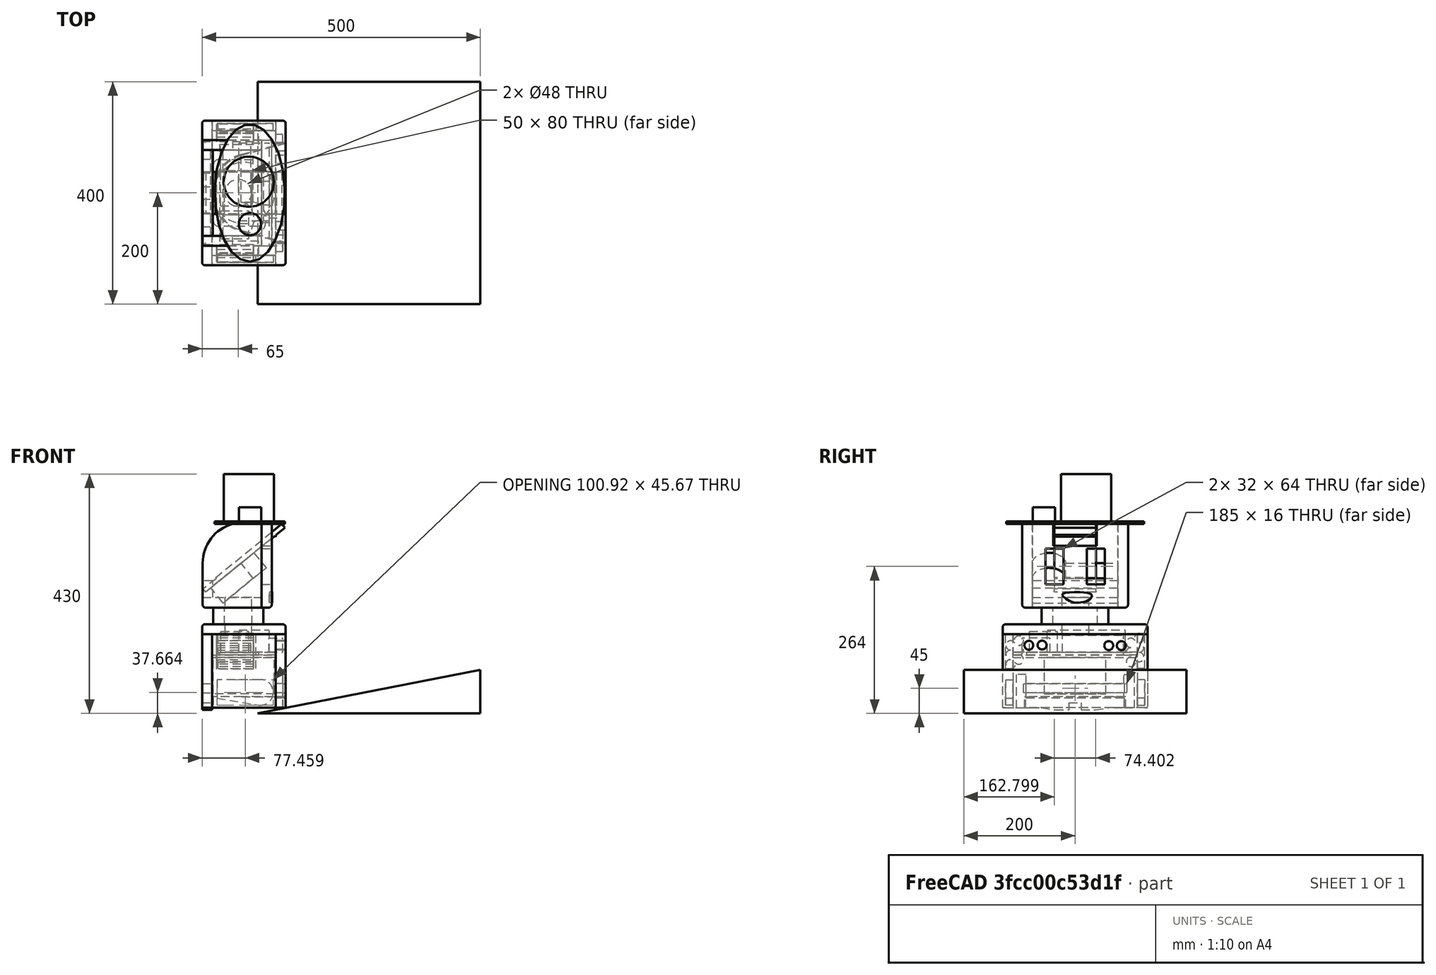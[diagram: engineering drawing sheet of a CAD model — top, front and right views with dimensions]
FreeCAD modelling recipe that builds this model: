
FCSTD DOCUMENT  (FreeCAD 0.17R13541 (Git))
Label: robot secondaire
License: All rights reserved
LicenseURL: http://en.wikipedia.org/wiki/All_rights_reserved
objects: Sketcher::SketchObject×22, PartDesign::Pad×21, TechDraw::DrawViewDimension×21, PartDesign::Body×20, TechDraw::DrawProjGroupItem×9, TechDraw::DrawProjGroup×9, PartDesign::Fillet×8, Part::Box×6, Part::Cylinder×5, PartDesign::FeatureBase×4, Part::Mirroring×1, App::DocumentObjectGroup×1, TechDraw::DrawSVGTemplate×1, TechDraw::DrawPage×1, PartDesign::Pocket×1
note: 110 computed .brp shape members not serialized (recipe doc carries the construction recipe); baked Part::Feature solids carry a one-line shape summary decoded from their .brp

FEATURE [Part::Cylinder] Cylinder  label="Arrêt urgence"
  Angle = 360
  AttacherType = Attacher::AttachEngine3D
  Height = 30
  Placement = pos=(86,-56,340) rot=(0,0,1;0rad)
  Radius = 20
FEATURE [Part::Cylinder] Cylinder001  label="Support balise"
  Angle = 360
  AttacherType = Attacher::AttachEngine3D
  Height = 90
  Placement = pos=(84,20,340) rot=(0,0,1;0rad)
  Radius = 45
FEATURE [Sketcher::SketchObject] Sketch002  label="Face avant002"
  AttachmentOffset = pos=(0,0,132) rot=(0,0,1;0rad)
  MapMode = 2
  Placement = pos=(132,0,0) rot=(0.57735,0.57735,0.57735;2.0944rad)
  sketch-geometry (17):
    g0: LineSegment StartX=-130 StartY=10 StartZ=0 EndX=-130 EndY=142 EndZ=0
    g1: LineSegment StartX=-130 StartY=142 StartZ=0 EndX=130 EndY=142 EndZ=0
    g2: LineSegment StartX=130 StartY=142 StartZ=0 EndX=130 EndY=10 EndZ=0
    g3: LineSegment StartX=130 StartY=10 StartZ=0 EndX=88.5 EndY=10 EndZ=0
    g4: LineSegment StartX=88.5 StartY=53 StartZ=0 EndX=-88.5 EndY=53 EndZ=0
    g5: LineSegment StartX=-88.5 StartY=53 StartZ=0 EndX=-88.5 EndY=37 EndZ=0
    g6: LineSegment StartX=88.5 StartY=53 StartZ=0 EndX=88.5 EndY=37 EndZ=0
    g7: LineSegment StartX=88.5 StartY=37 StartZ=0 EndX=-88.5 EndY=37 EndZ=0
    g8: LineSegment StartX=-88.5 StartY=10 StartZ=0 EndX=-88.5 EndY=28 EndZ=0
    g9: LineSegment StartX=-88.5 StartY=28 StartZ=0 EndX=88.5 EndY=28 EndZ=0
    g10: LineSegment StartX=88.5 StartY=28 StartZ=0 EndX=88.5 EndY=10 EndZ=0
    g11: Circle CenterX=-83.2022 CenterY=122.196 CenterZ=0 NormalX=0 NormalY=0 NormalZ=1 AngleXU=0 Radius=8
    g12: Circle CenterX=-59.3183 CenterY=122.573 CenterZ=0 NormalX=0 NormalY=0 NormalZ=1 AngleXU=0 Radius=8
    g13: Circle CenterX=60.4116 CenterY=121.713 CenterZ=0 NormalX=0 NormalY=0 NormalZ=1 AngleXU=0 Radius=8
    g14: Circle CenterX=82.9519 CenterY=121.552 CenterZ=0 NormalX=0 NormalY=0 NormalZ=1 AngleXU=0 Radius=8
    g15: LineSegment StartX=-130 StartY=10 StartZ=0 EndX=-88.5 EndY=10 EndZ=0
    g16: LineSegment StartX=-130 StartY=100 StartZ=0 EndX=130 EndY=100 EndZ=0
  constraints (41):
    c: Vertical(g0)
    c: Horizontal(g1)
    c: Coincident(g1,g2)
    c: Vertical(g2)
    c: Coincident(g2,g3)
    c: Horizontal(g3)
    c: DistanceY(g0,g0) = 132
    c: Symmetric(g4,g4,g-2)
    c: DistanceX(g1,g1) = 260
    c: Equal(g0,g2)
    c: DistanceX(g4,g4) = 177
    c: Coincident(g5,g4)
    c: Vertical(g5)
    c: Coincident(g6,g4)
    c: Vertical(g6)
    c: Coincident(g7,g6)
    c: Coincident(g7,g5)
    c: Horizontal(g7)
    c: Vertical(g8)
    c: Horizontal(g9)
    c: Coincident(g10,g9)
    c: Coincident(g10,g3)
    c: Vertical(g10)
    c: Equal(g4,g7)
    c: Coincident(g9,g8)
    c: Symmetric(g9,g8,g-2)
    c: Radius(g11) = 8
    c: Coincident(g0,g1)
    c: Coincident(g15,g0)
    c: Coincident(g15,g8)
    c: Horizontal(g15)
    c: Equal(g15,g3)
    c: DistanceY(g-1,g8) = 10
    c: PointOnObject(g16,g0)
    c: PointOnObject(g16,g2)
    c: Horizontal(g16)
    c: DistanceY(g-1,g16) = 100
    c: DistanceY(g4,g16) = 47
    c: DistanceY(g6,g16) = 63
    c: DistanceY(g-1,g9) = 28
    c: Equal(g9,g4)
FEATURE [Part::Cylinder] Cylinder002  label="Oreille"
  Angle = 360
  AttacherType = Attacher::AttachEngine3D
  Height = 5
  Placement = pos=(76,100,290) rot=(1,0,0;1.5708rad)
  Radius = 30
FEATURE [Sketcher::SketchObject] Sketch003  label="Bouche002"
  AttachmentOffset = pos=(0,5,-10) rot=(0,0,1;0rad)
  MapMode = 5
  Placement = pos=(-10,2e-12,5) rot=(0.57735,0.57735,0.57735;2.0944rad)
  Support = -> [YZ_Plane001]
  sketch-geometry (13):
    g0-g6: Circle [constr] x7 (B-spline internal-alignment scaffolding for g7; pole/knot coordinates omitted)
    g7: BSplineCurve PolesCount=7 KnotsCount=5 Degree=3 IsPeriodic=0
    g8-g12: GeomPoint [constr] x5 (B-spline internal-alignment scaffolding for g7; pole/knot coordinates omitted)
  constraints (5):
    c: Radius(g0) = 4
    c: Equal(g0, g1-g6) x6
    c: Coincident(g6,g0)
    c: InternalAlignment(g0-g6 -> g7) x7
    c: InternalAlignment(g8-g12 -> g7) x5
FEATURE [Part::Box] Box005  label="Oeil"
  AttacherType = Attacher::AttachEngine3D
  Height = 64.5
  Length = 25
  Placement = pos=(103,-53,232) rot=(0,0,1;0rad)
  Width = 32
FEATURE [Sketcher::SketchObject] Sketch004  label="Chapeau002"
  AttachmentOffset = pos=(0,0,340) rot=(0,0,1;0rad)
  MapMode = 5
  Placement = pos=(0,0,340) rot=(0,0,1;0rad)
  Support = -> [XY_Plane002]
  sketch-geometry (5):
    g0: Ellipse CenterX=85.6089 CenterY=0 CenterZ=0 NormalX=0 NormalY=0 NormalZ=1 MajorRadius=123.648 MinorRadius=62.9342 AngleXU=-1.5708
    g1: LineSegment [constr] StartX=85.6089 StartY=-123.648 StartZ=0 EndX=85.6089 EndY=123.648 EndZ=0
    g2: LineSegment [constr] StartX=148.543 StartY=0 StartZ=0 EndX=22.6748 EndY=0 EndZ=0
    g3: GeomPoint X=85.6089 Y=-106.433 Z=0
    g4: GeomPoint X=85.6089 Y=106.433 Z=0
  constraints (3):
    c: InternalAlignment(g1-g4 -> g0) x4
    c: Horizontal(g2)
    c: PointOnObject(g0,g-1)
FEATURE [PartDesign::Pad] Pad  label="Chapeau001"
  Length = 5
  Length2 = 100
  Profile = -> Sketch004
  Type = 0
FEATURE [PartDesign::Body] Body002  label="Chapeau"
  Group = -> [Sketch004,Pad]
  Origin = -> Origin002
  Tip = -> Pad
FEATURE [PartDesign::Pad] Pad002  label="Face avant001"
  Length = 18
  Length2 = 100
  Placement = pos=(132,0,0) rot=(0.57735,0.57735,0.57735;2.0944rad)
  Profile = -> Sketch002
  Type = 0
FEATURE [PartDesign::Pad] Pad003  label="Bouche001"
  Length = 5
  Length2 = 100
  Placement = pos=(0,0,0) rot=(0.57735,0.57735,0.57735;2.0944rad)
  Profile = -> Sketch003
  Type = 0
FEATURE [PartDesign::Body] Body001  label="Bouche"
  Group = -> [Sketch003,Pad003]
  Origin = -> Origin001
  Placement = pos=(131,0,0) rot=(0,0,1;0rad)
  Tip = -> Pad003
FEATURE [Sketcher::SketchObject] Sketch005  label="Téléphone002"
  AttachmentOffset = pos=(2,0,0) rot=(0,0,1;0rad)
  MapMode = 5
  Placement = pos=(2,0,0) rot=(1,0,0;1.5708rad)
  Support = -> [XZ_Plane004]
  sketch-geometry (13):
    g0: LineSegment StartX=4.40524 StartY=217.84 StartZ=0 EndX=0 EndY=223.28 EndZ=0
    g1: LineSegment StartX=22.0557 StartY=243.714 StartZ=0 EndX=140.959 EndY=340 EndZ=0
    g2: LineSegment StartX=140.959 StartY=340 StartZ=0 EndX=146.623 EndY=333.006 EndZ=0
    g3: LineSegment StartX=128.749 StartY=318.531 StartZ=0 EndX=4.40524 EndY=217.84 EndZ=0
    g4: LineSegment StartX=128.749 StartY=318.531 StartZ=0 EndX=129.378 EndY=317.754 EndZ=0
    g5: LineSegment StartX=129.378 StartY=317.754 StartZ=0 EndX=131.709 EndY=319.642 EndZ=0
    g6: LineSegment StartX=131.709 StartY=319.642 StartZ=0 EndX=131.08 EndY=320.419 EndZ=0
    g7: LineSegment StartX=131.08 StartY=320.419 StartZ=0 EndX=146.623 EndY=333.006 EndZ=0
    g8: LineSegment [constr] StartX=128.909 StartY=320.717 StartZ=0 EndX=179.705 EndY=0 EndZ=0
    g9: LineSegment [constr] StartX=128.909 StartY=320.717 StartZ=0 EndX=964.406 EndY=0 EndZ=0
    g10: LineSegment [constr] StartX=128.909 StartY=320.717 StartZ=0 EndX=130.544 EndY=318.698 EndZ=0
    g11: LineSegment StartX=22.0557 StartY=243.714 StartZ=0 EndX=23.3144 EndY=242.16 EndZ=0
    g12: LineSegment StartX=23.3144 StartY=242.16 StartZ=0 EndX=0 EndY=223.28 EndZ=0
  constraints (40):
    c: Coincident(g1,g2)
    c: Parallel(g1,g3)
    c: Parallel(g0,g2)
    c: Perpendicular(g1,g0)
    c: Coincident(g3,g0)
    c: Coincident(g3,g4)
    c: Coincident(g4,g5)
    c: Coincident(g5,g6)
    c: Coincident(g6,g7)
    c: Coincident(g7,g2)
    c: Parallel(g7,g1)
    c: Parallel(g5,g1)
    c: Distance(g5) = 3
    c: Perpendicular(g7,g6)
    c: Perpendicular(g4,g3)
    c: Equal(g6,g4)
    c: Distance(g6) = 1
    c: Distance(g7) = 20
    c: Coincident(g9,g8)
    c: Angle(g8,g9) = 1.0472
    c: PointOnObject(g5,g9)
    c: PointOnObject(g4,g8)
    c: Coincident(g10,g8)
    c: PointOnObject(g10,g5)
    c: Perpendicular(g10,g5)
    c: Symmetric(g5,g5,g10)
    c: Coincident(g12,g11)
    c: Perpendicular(g1,g11)
    c: Coincident(g1,g11)
    c: Distance(g2) = 9
    c: Coincident(g0,g12)
    c: Parallel(g12,g3)
    c: Distance(g12) = 30
    c: Distance(g0) = 7
    c: Distance(g1) = 153
    c: Angle(g-1,g3) = 0.680678
    c: DistanceY(g-1,g1) = 340
    c: PointOnObject(g0,g-2)
    c: PointOnObject(g9,g-1)
    c: PointOnObject(g8,g-1)
FEATURE [PartDesign::Pad] Pad004  label="Téléphone001"
  Length = 75
  Length2 = 100
  Midplane = true
  Placement = pos=(0,0,0) rot=(1,0,0;1.5708rad)
  Profile = -> Sketch005
  Type = 0
FEATURE [PartDesign::Body] Body004  label="Téléphone"
  Group = -> [Sketch005,Pad004]
  Origin = -> Origin004
  Tip = -> Pad004
FEATURE [Sketcher::SketchObject] Sketch006  label="Cou002"
  AttachmentOffset = pos=(0,0,160) rot=(0,0,1;0rad)
  MapMode = 5
  Placement = pos=(0,0,160) rot=(0,0,1;0rad)
  Support = -> [XY_Plane005]
  sketch-geometry (8):
    g0: LineSegment StartX=20 StartY=60 StartZ=0 EndX=110 EndY=60 EndZ=0
    g1: LineSegment StartX=110 StartY=60 StartZ=0 EndX=110 EndY=-60 EndZ=0
    g2: LineSegment StartX=110 StartY=-60 StartZ=0 EndX=20 EndY=-60 EndZ=0
    g3: LineSegment StartX=20 StartY=-60 StartZ=0 EndX=20 EndY=60 EndZ=0
    g4: LineSegment StartX=40 StartY=40 StartZ=0 EndX=90 EndY=40 EndZ=0
    g5: LineSegment StartX=90 StartY=40 StartZ=0 EndX=90 EndY=-40 EndZ=0
    g6: LineSegment StartX=90 StartY=-40 StartZ=0 EndX=40 EndY=-40 EndZ=0
    g7: LineSegment StartX=40 StartY=-40 StartZ=0 EndX=40 EndY=40 EndZ=0
  constraints (24):
    c: Coincident(g0,g1)
    c: Coincident(g1,g2)
    c: Coincident(g2,g3)
    c: Coincident(g3,g0)
    c: Horizontal(g0)
    c: Horizontal(g2)
    c: Vertical(g1)
    c: Vertical(g3)
    c: Coincident(g4,g5)
    c: Coincident(g5,g6)
    c: Coincident(g6,g7)
    c: Coincident(g7,g4)
    c: Horizontal(g4)
    c: Horizontal(g6)
    c: Vertical(g5)
    c: Vertical(g7)
    c: DistanceX(g0,g4) = 20
    c: DistanceX(g4,g0) = 20
    c: DistanceX(g0,g0) = 90
    c: DistanceY(g1,g1) = 120
    c: DistanceY(g4,g0) = 20
    c: Symmetric(g0,g2,g-1)
    c: DistanceX(g-1,g0) = 20
    c: DistanceY(g1,g5) = 20
FEATURE [PartDesign::Pad] Pad005  label="Cou001"
  Length = 30
  Length2 = 100
  Profile = -> Sketch006
  Type = 0
FEATURE [PartDesign::Fillet] Fillet003  label="Fillet cou"
  Base = -> Pad005 [Edge5,Edge2,Edge8,Edge1]
  BaseFeature = -> Pad005
  Radius = 10
FEATURE [PartDesign::Body] Body005  label="Cou"
  Group = -> [Sketch006,Pad005,Fillet003]
  Origin = -> Origin005
  Tip = -> Fillet003
FEATURE [Part::Box] Box006  label="Ultrason"
  AttacherType = Attacher::AttachEngine3D
  Height = 25
  Length = 25
  Placement = pos=(120,45,110) rot=(0,0,1;0rad)
  Width = 50
FEATURE [Part::Mirroring] Part__Mirroring003  label="Ultrason (Mirror)"
  Base = (0,0,0)
  Normal = (0,1,0)
  Source = -> Box006
FEATURE [Part::Box] Box008  label="Pont H"
  AttacherType = Attacher::AttachEngine3D
  Height = 37
  Length = 50
  Placement = pos=(34,-82,110) rot=(0,0,1;0rad)
  Width = 50
FEATURE [Part::Box] Box009  label="Arduino Uno"
  AttacherType = Attacher::AttachEngine3D
  Height = 40
  Length = 55
  Placement = pos=(66,-50,110) rot=(0,0,1;0rad)
  Width = 140
FEATURE [Part::Box] Box010  label="Arduino nano et alim 5V"
  AttacherType = Attacher::AttachEngine3D
  Height = 30
  Length = 55
  Placement = pos=(33,-23,110) rot=(0,0,1;0rad)
  Width = 110
FEATURE [Part::Cylinder] Cylinder003  label="LIDAR"
  Angle = 360
  AttacherType = Attacher::AttachEngine3D
  Height = 65
  Placement = pos=(75,0,35) rot=(0,0,1;0rad)
  Radius = 55
FEATURE [Part::Box] Box011  label="Plaque électronique"
  AttacherType = Attacher::AttachEngine3D
  Height = 5
  Length = 114
  Placement = pos=(18,-112,100) rot=(0,0,1;0rad)
  Width = 224
  expr: Placement.Base.y = Width / -2
FEATURE [Sketcher::SketchObject] Sketch037  label="batterie"
  MapMode = 5
  Placement = pos=(26.5,115,101) rot=(0.707107,0,0.707107;3.14159rad)
  expr: Constraints[27] = batterie.Constraints.pileRayon * 2
  expr: Constraints.pileRayon = 33.899999999999999 / 4
  sketch-geometry (12):
    g0: ArcOfCircle CenterX=33.9 CenterY=0 CenterZ=0 NormalX=0 NormalY=0 NormalZ=1 AngleXU=0 Radius=8.475 StartAngle=3.14159 EndAngle=8.37758
    g1: ArcOfCircle CenterX=8.475 CenterY=14.6791 CenterZ=0 NormalX=0 NormalY=0 NormalZ=1 AngleXU=0 Radius=8.475 StartAngle=6.072e-09 EndAngle=3.14159
    g2: ArcOfCircle CenterX=25.425 CenterY=14.6791 CenterZ=0 NormalX=0 NormalY=0 NormalZ=1 AngleXU=0 Radius=8.475 StartAngle=5.23599 EndAngle=9.42478
    g3: ArcOfCircle CenterX=-8.475 CenterY=14.6791 CenterZ=0 NormalX=0 NormalY=0 NormalZ=1 AngleXU=0 Radius=8.475 StartAngle=6.31e-09 EndAngle=5.23599
    g4: ArcOfCircle CenterX=16.95 CenterY=0 CenterZ=0 NormalX=0 NormalY=0 NormalZ=1 AngleXU=0 Radius=8.475 StartAngle=3.14159 EndAngle=6.28319
    g5: ArcOfCircle CenterX=0 CenterY=0 CenterZ=0 NormalX=0 NormalY=0 NormalZ=1 AngleXU=0 Radius=8.475 StartAngle=2.0944 EndAngle=6.28319
    g6: LineSegment [constr] StartX=33.9 StartY=0 StartZ=0 EndX=25.425 EndY=14.6791 EndZ=0
    g7: LineSegment [constr] StartX=25.425 StartY=14.6791 StartZ=0 EndX=16.95 EndY=0 EndZ=0
    g8: LineSegment [constr] StartX=16.95 StartY=0 StartZ=0 EndX=8.475 EndY=14.6791 EndZ=0
    g9: LineSegment [constr] StartX=8.475 StartY=14.6791 StartZ=0 EndX=0 EndY=0 EndZ=0
    g10: LineSegment [constr] StartX=0 StartY=0 StartZ=0 EndX=-8.475 EndY=14.6791 EndZ=0
    g11: LineSegment [constr] StartX=-8.475 StartY=14.6791 StartZ=0 EndX=25.425 EndY=14.6791 EndZ=0
  constraints (34):
    c: Radius(g0) = 8.475  'pileRayon'
    c: Equal(g0,g1)
    c: Equal(g0,g2)
    c: Equal(g0,g3)
    c: Coincident(g0,g4)
    c: Coincident(g1,g3)
    c: Coincident(g5,g3)
    c: Coincident(g2,g1)
    c: Coincident(g4,g5)
    c: Coincident(g0,g2)
    c: Equal(g4,g5)
    c: Equal(g5,g3)
    c: PointOnObject(g0,g-1)
    c: Coincident(g6,g0)
    c: Coincident(g6,g2)
    c: Coincident(g7,g2)
    c: Coincident(g7,g4)
    c: Coincident(g7,g8)
    c: Coincident(g8,g1)
    c: Coincident(g8,g9)
    c: Coincident(g9,g5)
    c: Coincident(g9,g10)
    c: Coincident(g3,g10)
    c: Parallel(g6,g8)
    c: Parallel(g8,g10)
    c: Parallel(g9,g7)
    c: Coincident(g5,g-1)
    c: Distance(g6) = 16.95
    c: Equal(g6,g7)
    c: Equal(g7,g8)
    c: Equal(g8,g9)
    c: Equal(g9,g10)
    c: Coincident(g11,g3)
    c: Coincident(g11,g2)
FEATURE [PartDesign::Pad] Pad006  label="Batterie"
  Length = 66
  Length2 = 100
  Placement = pos=(26.5,115,101) rot=(0.707107,0,0.707107;3.14159rad)
  Profile = -> Sketch037
  Type = 0
FEATURE [PartDesign::Body] Body006  label="Batterie001"
  Group = -> [Sketch037,Pad006]
  Origin = -> Origin006
  Tip = -> Pad006
FEATURE [PartDesign::FeatureBase] Clone  label="Batterie002"
  BaseFeature = -> Pad006
  Placement = pos=(26.5,-116,122) rot=(0,1,0;1.5708rad)
FEATURE [PartDesign::Body] CloneBody  label="Batterie003"
  BaseFeature = -> Pad006
  Group = -> [Clone]
  Origin = -> Origin008
  Tip = -> Clone
FEATURE [Sketcher::SketchObject] Sketch038  label="porte électronique"
  AttachmentOffset = pos=(0,0,105) rot=(0,0,1;0rad)
  MapMode = 5
  Placement = pos=(0,0,105) rot=(0,0,1;0rad)
  Support = -> [XY_Plane009]
  sketch-geometry (8):
    g0: LineSegment StartX=132 StartY=-112 StartZ=0 EndX=102 EndY=-112 EndZ=0
    g1: LineSegment StartX=102 StartY=-112 StartZ=0 EndX=102 EndY=-87 EndZ=0
    g2: LineSegment StartX=102 StartY=-87 StartZ=0 EndX=32 EndY=-87 EndZ=0
    g3: LineSegment StartX=32 StartY=-87 StartZ=0 EndX=32 EndY=87 EndZ=0
    g4: LineSegment StartX=32 StartY=87 StartZ=0 EndX=102 EndY=87 EndZ=0
    g5: LineSegment StartX=102 StartY=87 StartZ=0 EndX=102 EndY=112 EndZ=0
    g6: LineSegment StartX=102 StartY=112 StartZ=0 EndX=132 EndY=112 EndZ=0
    g7: LineSegment StartX=132 StartY=112 StartZ=0 EndX=132 EndY=-112 EndZ=0
  constraints (24):
    c: Horizontal(g4)
    c: Coincident(g5,g4)
    c: Coincident(g6,g5)
    c: Vertical(g5)
    c: Horizontal(g6)
    c: Coincident(g6,g7)
    c: Vertical(g7)
    c: Coincident(g0,g7)
    c: Coincident(g0,g1)
    c: Coincident(g1,g2)
    c: Vertical(g1)
    c: Horizontal(g0)
    c: Horizontal(g2)
    c: Coincident(g2,g3)
    c: Equal(g5,g1)
    c: Equal(g6,g0)
    c: Equal(g4,g2)
    c: Coincident(g3,g4)
    c: Symmetric(g3,g2,g-1)
    c: DistanceX(g3,g6) = 100
    c: DistanceX(g-1,g6) = 132
    c: DistanceY(g-1,g6) = 112
    c: DistanceY(g5,g5) = 25
    c: DistanceX(g6,g6) = 30
FEATURE [PartDesign::Pad] Pad007
  Length = 5
  Length2 = 100
  Profile = -> Sketch038
  Type = 0
FEATURE [PartDesign::Body] Body007  label="Porte électronique"
  Group = -> [Sketch038,Pad007]
  Origin = -> Origin009
  Tip = -> Pad007
FEATURE [Sketcher::SketchObject] Sketch039  label="Pente002"
  MapMode = 5
  Placement = pos=(0,0,0) rot=(1,0,0;1.5708rad)
  Support = -> [XZ_Plane010]
  sketch-geometry (3):
    g0: LineSegment StartX=100 StartY=0 StartZ=0 EndX=500 EndY=77.7521 EndZ=0
    g1: LineSegment StartX=500 StartY=77.7521 StartZ=0 EndX=500 EndY=0 EndZ=0
    g2: LineSegment StartX=500 StartY=0 StartZ=0 EndX=100 EndY=0 EndZ=0
  constraints (9):
    c: PointOnObject(g0,g-1)
    c: Coincident(g1,g0)
    c: Vertical(g1)
    c: Coincident(g2,g1)
    c: Coincident(g2,g0)
    c: Horizontal(g2)
    c: DistanceX(g2,g2) = 400
    c: Angle(g2,g0) = 0.191986
    c: DistanceX(g-1,g0) = 100
FEATURE [PartDesign::Pad] Pad008  label="Pente001"
  Length = 400
  Length2 = 100
  Midplane = true
  Placement = pos=(0,0,0) rot=(1,0,0;1.5708rad)
  Profile = -> Sketch039
  Type = 0
FEATURE [PartDesign::Body] Body008  label="Pente"
  Group = -> [Sketch039,Pad008]
  Origin = -> Origin010
  Tip = -> Pad008
FEATURE [Sketcher::SketchObject] Sketch040
  AttachmentOffset = pos=(0,0,125) rot=(0,0,1;0rad)
  MapMode = 5
  Placement = pos=(0,-125,-1.3e-11) rot=(1,0,0;1.5708rad)
  Support = -> [XZ_Plane011]
  expr: Constraints[6] = 75 / 2
  expr: Constraints[8] = 45 - 18
  expr: Constraints[10] = 46 / 2
  sketch-geometry (15):
    g0: LineSegment StartX=18 StartY=10 StartZ=0 EndX=132 EndY=10 EndZ=0
    g1: LineSegment StartX=132 StartY=10 StartZ=0 EndX=132 EndY=142 EndZ=0
    g2: Circle [constr] CenterX=105 CenterY=37.5 CenterZ=0 NormalX=0 NormalY=0 NormalZ=1 AngleXU=0 Radius=37.5
    g3: Circle [constr] CenterX=105 CenterY=37.5 CenterZ=0 NormalX=0 NormalY=0 NormalZ=1 AngleXU=0 Radius=23
    g4: LineSegment StartX=105 StartY=60.5 StartZ=0 EndX=27 EndY=60.5 EndZ=0
    g5: ArcOfCircle CenterX=105 CenterY=37.5 CenterZ=0 NormalX=0 NormalY=0 NormalZ=1 AngleXU=0 Radius=23 StartAngle=4.54308 EndAngle=7.85398
    g6: LineSegment [constr] StartX=105 StartY=60.5 StartZ=0 EndX=105 EndY=37.5 EndZ=0
    g7: LineSegment StartX=27 StartY=60.5 StartZ=0 EndX=27 EndY=27.5 EndZ=0
    g8: LineSegment StartX=27 StartY=27.5 StartZ=0 EndX=101.125 EndY=14.8289 EndZ=0
    g9: LineSegment StartX=28 StartY=142 StartZ=0 EndX=28 EndY=80.5 EndZ=0
    g10: LineSegment StartX=28 StartY=80.5 StartZ=0 EndX=97 EndY=80.5 EndZ=0
    g11: LineSegment StartX=97 StartY=80.5 StartZ=0 EndX=97 EndY=142 EndZ=0
    g12: LineSegment StartX=18 StartY=142 StartZ=0 EndX=18 EndY=10 EndZ=0
    g13: LineSegment StartX=18 StartY=142 StartZ=0 EndX=28 EndY=142 EndZ=0
    g14: LineSegment StartX=97 StartY=142 StartZ=0 EndX=132 EndY=142 EndZ=0
  constraints (43):
    c: Horizontal(g0)
    c: Vertical(g1)
    c: Coincident(g1,g0)
    c: DistanceY(g-1,g0) = 10
    c: DistanceX(g0,g0) = 114
    c: DistanceX(g-1,g0) = 18
    c: Radius(g2) = 37.5
    c: DistanceY(g-1,g2) = 37.5
    c: DistanceX(g2,g0) = 27
    c: Coincident(g3,g2)
    c: Radius(g3) = 23
    c: PointOnObject(g4,g3)
    c: Horizontal(g4)
    c: DistanceX(g4,g4) = 78
    c: Coincident(g5,g2)
    c: Coincident(g5,g4)
    c: Coincident(g6,g4)
    c: Coincident(g6,g2)
    c: Vertical(g6)
    c: Coincident(g7,g4)
    c: Vertical(g7)
    c: Coincident(g8,g7)
    c: Coincident(g8,g5)
    c: Tangent(g8,g3)
    c: DistanceY(g7,g7) = 33
    c: Vertical(g9)
    c: DistanceY(g4,g9) = 20
    c: Coincident(g10,g9)
    c: Horizontal(g10)
    c: Vertical(g11)
    c: Coincident(g10,g11)
    c: DistanceX(g10,g10) = 69
    c: Coincident(g12,g0)
    c: Vertical(g12)
    c: Coincident(g13,g12)
    c: Coincident(g13,g9)
    c: Horizontal(g13)
    c: Coincident(g14,g11)
    c: Horizontal(g14)
    c: Coincident(g14,g1)
    c: DistanceY(g1,g1) = 132
    c: Equal(g12,g1)
    c: DistanceX(g13,g13) = 10
FEATURE [Sketcher::SketchObject] Sketch041
  AttachmentOffset = pos=(0,0,125) rot=(0,0,1;0rad)
  MapMode = 5
  Placement = pos=(0,-125,-1.3e-11) rot=(1,0,0;1.5708rad)
  Support = -> [XZ_Plane011]
  sketch-geometry (4):
    g0: LineSegment StartX=18 StartY=10 StartZ=0 EndX=132 EndY=10 EndZ=0
    g1: LineSegment StartX=132 StartY=10 StartZ=0 EndX=132 EndY=142 EndZ=0
    g2: LineSegment StartX=132 StartY=142 StartZ=0 EndX=18 EndY=142 EndZ=0
    g3: LineSegment StartX=18 StartY=142 StartZ=0 EndX=18 EndY=10 EndZ=0
  constraints (12):
    c: Coincident(g0,g1)
    c: Coincident(g1,g2)
    c: Coincident(g2,g3)
    c: Coincident(g3,g0)
    c: Horizontal(g0)
    c: Horizontal(g2)
    c: Vertical(g1)
    c: Vertical(g3)
    c: DistanceY(g3,g3) = 132
    c: DistanceY(g-1,g0) = 10
    c: DistanceX(g-1,g0) = 18
    c: DistanceX(g0,g0) = 114
FEATURE [PartDesign::Pad] Pad009  label="Corps droit interieur"
  Length = 13
  Length2 = 100
  Placement = pos=(0,0,0) rot=(1,0,0;1.5708rad)
  Profile = -> Sketch040
  Reversed = true
  Type = 0
FEATURE [PartDesign::Pad] Pad010  label="Corps droite extérieur"
  BaseFeature = -> Pad009
  Length = 5
  Length2 = 100
  Placement = pos=(0,0,0) rot=(1,0,0;1.5708rad)
  Profile = -> Sketch041
  Type = 0
FEATURE [PartDesign::Body] Body009  label="Corps droite"
  Group = -> [Sketch040,Sketch041,Pad009,Pad010]
  Origin = -> Origin011
  Tip = -> Pad010
FEATURE [Part::Cylinder] Cylinder004  label="Roue001"
  Angle = 360
  AttacherType = Attacher::AttachEngine3D
  Height = 14
  Placement = pos=(105,-90,37.5) rot=(1,0,0;1.5708rad)
  Radius = 37.5
  expr: Placement.Base.z = Radius
  expr: Radius = 75 / 2
FEATURE [Sketcher::SketchObject] Sketch042  label="Face arriere002"
  AttachmentOffset = pos=(0,0,132) rot=(0,0,1;0rad)
  MapMode = 2
  Placement = pos=(0,0,0) rot=(0.57735,0.57735,0.57735;2.0944rad)
  sketch-geometry (17):
    g0: LineSegment StartX=-130 StartY=10 StartZ=0 EndX=-130 EndY=142 EndZ=0
    g1: LineSegment StartX=-130 StartY=142 StartZ=0 EndX=130 EndY=142 EndZ=0
    g2: LineSegment StartX=130 StartY=142 StartZ=0 EndX=130 EndY=10 EndZ=0
    g3: LineSegment StartX=130 StartY=10 StartZ=0 EndX=60.6779 EndY=10 EndZ=0
    g4: LineSegment StartX=-130 StartY=10 StartZ=0 EndX=-60.6779 EndY=10 EndZ=0
    g5: LineSegment StartX=-130 StartY=100 StartZ=0 EndX=130 EndY=100 EndZ=0
    g6: LineSegment StartX=-60.6779 StartY=10 StartZ=0 EndX=-36 EndY=6 EndZ=0
    g7: LineSegment StartX=-11 StartY=19 StartZ=0 EndX=11 EndY=19 EndZ=0
    g8: LineSegment StartX=36 StartY=6 StartZ=0 EndX=60.6779 EndY=10 EndZ=0
    g9: LineSegment StartX=-36 StartY=6 StartZ=0 EndX=-11 EndY=6 EndZ=0
    g10: LineSegment StartX=-11 StartY=6 StartZ=0 EndX=-11 EndY=19 EndZ=0
    g11: LineSegment StartX=11 StartY=19 StartZ=0 EndX=11 EndY=6 EndZ=0
    g12: LineSegment StartX=11 StartY=6 StartZ=0 EndX=36 EndY=6 EndZ=0
    g13: LineSegment StartX=-92.5 StartY=53 StartZ=0 EndX=92.5 EndY=53 EndZ=0
    g14: LineSegment StartX=92.5 StartY=53 StartZ=0 EndX=92.5 EndY=37 EndZ=0
    g15: LineSegment StartX=92.5 StartY=37 StartZ=0 EndX=-92.5 EndY=37 EndZ=0
    g16: LineSegment StartX=-92.5 StartY=37 StartZ=0 EndX=-92.5 EndY=53 EndZ=0
  constraints (52):
    c: Vertical(g0)
    c: Horizontal(g1)
    c: Coincident(g1,g2)
    c: Vertical(g2)
    c: Coincident(g2,g3)
    c: Horizontal(g3)
    c: DistanceY(g0,g0) = 132
    c: DistanceX(g1,g1) = 260
    c: Equal(g0,g2)
    c: Coincident(g0,g1)
    c: Coincident(g4,g0)
    c: Horizontal(g4)
    c: Equal(g4,g3)
    c: DistanceY(g-1,g4) = 10
    c: PointOnObject(g5,g0)
    c: PointOnObject(g5,g2)
    c: Horizontal(g5)
    c: DistanceY(g-1,g5) = 100
    c: Symmetric(g0,g2,g-2)
    c: Horizontal(g7)
    c: Coincident(g8,g3)
    c: Symmetric(g7,g7,g-2)
    c: Coincident(g6,g4)
    c: DistanceY(g-1,g6) = 6
    c: Coincident(g9,g6)
    c: Horizontal(g9)
    c: Coincident(g10,g9)
    c: Coincident(g10,g7)
    c: Coincident(g11,g7)
    c: Coincident(g12,g11)
    c: Coincident(g12,g8)
    c: Horizontal(g12)
    c: Equal(g12,g9)
    c: DistanceX(g9,g9) = 25
    c: Vertical(g10)
    c: Vertical(g11)
    c: Equal(g11,g10)
    c: DistanceX(g7,g7) = 22
    c: Equal(g8,g12)
    c: DistanceY(g11,g11) = 13
    c: Coincident(g13,g14)
    c: Coincident(g14,g15)
    c: Coincident(g15,g16)
    c: Coincident(g16,g13)
    c: Horizontal(g13)
    c: Horizontal(g15)
    c: Vertical(g14)
    c: Vertical(g16)
    c: DistanceY(g13,g5) = 47
    c: DistanceY(g14,g5) = 63
    c: DistanceX(g13,g13) = 185
    c: Symmetric(g13,g13,g-2)
FEATURE [PartDesign::Pad] Pad011  label="Face arriere001"
  Length = 18
  Length2 = 100
  Placement = pos=(0,0,0) rot=(0.57735,0.57735,0.57735;2.0944rad)
  Profile = -> Sketch042
  Type = 0
FEATURE [Sketcher::SketchObject] Sketch043  label="Collecteur palets002"
  AttachmentOffset = pos=(0,0,10) rot=(0,0,1;0rad)
  MapMode = 5
  Placement = pos=(0,0,10) rot=(0,0,1;0rad)
  Support = -> [XY_Plane013]
  expr: Constraints[20] = 72 + 18
  sketch-geometry (8):
    g0: ArcOfCircle CenterX=90 CenterY=0 CenterZ=0 NormalX=0 NormalY=0 NormalZ=1 AngleXU=0 Radius=70 StartAngle=1.8326 EndAngle=4.45059
    g1: ArcOfCircle CenterX=90 CenterY=0 CenterZ=0 NormalX=0 NormalY=0 NormalZ=1 AngleXU=0 Radius=72 StartAngle=1.8326 EndAngle=4.45059
    g2: LineSegment StartX=71.365 StartY=69.5467 StartZ=0 EndX=150 EndY=90.6168 EndZ=0
    g3: LineSegment StartX=150 StartY=90.6168 StartZ=0 EndX=150 EndY=88.6168 EndZ=0
    g4: LineSegment StartX=150 StartY=88.6168 StartZ=0 EndX=71.8827 EndY=67.6148 EndZ=0
    g5: LineSegment StartX=71.8827 StartY=-67.6148 StartZ=0 EndX=150.018 EndY=-88.551 EndZ=0
    g6: LineSegment StartX=150.018 StartY=-88.551 StartZ=0 EndX=150.018 EndY=-90.551 EndZ=0
    g7: LineSegment StartX=150.018 StartY=-90.551 StartZ=0 EndX=71.365 EndY=-69.5467 EndZ=0
  constraints (22):
    c: Symmetric(g0,g0,g-1)
    c: Symmetric(g1,g1,g-1)
    c: Radius(g0) = 70
    c: Radius(g1) = 72
    c: Angle(g0) = 2.61799
    c: Angle(g1) = 2.61799
    c: Coincident(g0,g1)
    c: Tangent(g1,g2) = 1.5708
    c: Coincident(g2,g3)
    c: Coincident(g3,g4)
    c: Coincident(g4,g0)
    c: Vertical(g3)
    c: DistanceY(g3,g3) = 2
    c: Tangent(g0,g5) = -1.5708
    c: Coincident(g5,g6)
    c: Vertical(g6)
    c: Coincident(g6,g7)
    c: Coincident(g7,g1)
    c: Equal(g6,g3)
    c: DistanceX(g-1,g3) = 150
    c: DistanceX(g-1,g0) = 90
    c: Equal(g5,g4)
FEATURE [PartDesign::Pad] Pad012  label="Collecteur palets001"
  Length = 20
  Length2 = 100
  Profile = -> Sketch043
  Type = 0
FEATURE [PartDesign::Body] Body011  label="Collecteur palets"
  Group = -> [Sketch043,Pad012]
  Origin = -> Origin013
  Tip = -> Pad012
FEATURE [Sketcher::SketchObject] Sketch045  label="Face dessus002"
  AttachmentOffset = pos=(0,0,142) rot=(0,0,1;0rad)
  MapMode = 5
  Placement = pos=(0,0,142) rot=(0,0,1;0rad)
  Support = -> [XY_Plane015]
  sketch-geometry (5):
    g0: LineSegment StartX=0 StartY=130 StartZ=0 EndX=150 EndY=130 EndZ=0
    g1: LineSegment StartX=150 StartY=130 StartZ=0 EndX=150 EndY=-130 EndZ=0
    g2: LineSegment StartX=150 StartY=-130 StartZ=0 EndX=0 EndY=-130 EndZ=0
    g3: LineSegment StartX=0 StartY=-130 StartZ=0 EndX=0 EndY=130 EndZ=0
    g4: Circle CenterX=65 CenterY=0 CenterZ=0 NormalX=0 NormalY=0 NormalZ=1 AngleXU=0 Radius=24
  constraints (15):
    c: Coincident(g0,g1)
    c: Coincident(g1,g2)
    c: Coincident(g2,g3)
    c: Coincident(g3,g0)
    c: Horizontal(g0)
    c: Horizontal(g2)
    c: Vertical(g1)
    c: Vertical(g3)
    c: PointOnObject(g0,g-2)
    c: Symmetric(g0,g2,g-1)
    c: DistanceY(g3,g3) = 260
    c: DistanceX(g0,g0) = 150
    c: PointOnObject(g4,g-1)
    c: Radius(g4) = 24
    c: DistanceX(g-1,g4) = 65
FEATURE [PartDesign::Pad] Pad013  label="Face dessus001"
  Length = 18
  Length2 = 100
  Profile = -> Sketch045
  Type = 0
FEATURE [PartDesign::Fillet] Fillet007  label="Fillet Face dessus"
  Base = -> Pad013 [Edge10,Edge7,Edge4,Edge12,Edge8,Edge5,Edge1,Edge2]
  BaseFeature = -> Pad013
  Radius = 5
FEATURE [PartDesign::Body] Body013  label="Face dessus"
  Group = -> [Sketch045,Pad013,Fillet007]
  Origin = -> Origin015
  Tip = -> Fillet007
FEATURE [Sketcher::SketchObject] Sketch046  label="Dessous tete002"
  AttachmentOffset = pos=(0,0,190) rot=(0,0,1;0rad)
  MapMode = 5
  Placement = pos=(0,0,190) rot=(0,0,1;0rad)
  Support = -> [XY_Plane016]
  sketch-geometry (5):
    g0: LineSegment StartX=1 StartY=77 StartZ=0 EndX=107 EndY=77 EndZ=0
    g1: LineSegment StartX=107 StartY=77 StartZ=0 EndX=107 EndY=-77 EndZ=0
    g2: LineSegment StartX=107 StartY=-77 StartZ=0 EndX=1 EndY=-77 EndZ=0
    g3: LineSegment StartX=1 StartY=-77 StartZ=0 EndX=1 EndY=77 EndZ=0
    g4: Circle CenterX=65 CenterY=0 CenterZ=0 NormalX=0 NormalY=0 NormalZ=1 AngleXU=0 Radius=24
  constraints (15):
    c: Coincident(g0,g1)
    c: Coincident(g1,g2)
    c: Coincident(g2,g3)
    c: Coincident(g3,g0)
    c: Horizontal(g0)
    c: Horizontal(g2)
    c: Vertical(g1)
    c: Vertical(g3)
    c: Symmetric(g0,g2,g-1)
    c: DistanceY(g3,g3) = 154
    c: DistanceX(g0,g0) = 106
    c: PointOnObject(g4,g-1)
    c: Radius(g4) = 24
    c: DistanceX(g-1,g4) = 65
    c: DistanceX(g-1,g0) = 1
FEATURE [PartDesign::Pad] Pad014  label="Dessous tete001"
  Length = 18
  Length2 = 100
  Profile = -> Sketch046
  Type = 0
FEATURE [Sketcher::SketchObject] Sketch047  label="Avant tete002"
  AttachmentOffset = pos=(0,190,107) rot=(0,0,1;0rad)
  MapMode = 5
  Placement = pos=(107,9e-12,190) rot=(0.57735,0.57735,0.57735;2.0944rad)
  Support = -> [YZ_Plane017]
  sketch-geometry (16):
    g0: LineSegment StartX=-95 StartY=0 StartZ=0 EndX=95 EndY=0 EndZ=0
    g1: LineSegment StartX=95 StartY=0 StartZ=0 EndX=95 EndY=150 EndZ=0
    g2: LineSegment StartX=-95 StartY=150 StartZ=0 EndX=-95 EndY=0 EndZ=0
    g3: LineSegment StartX=39 StartY=150 StartZ=0 EndX=39 EndY=111 EndZ=0
    g4: LineSegment StartX=39 StartY=111 StartZ=0 EndX=-39 EndY=111 EndZ=0
    g5: LineSegment StartX=-39 StartY=111 StartZ=0 EndX=-39 EndY=150 EndZ=0
    g6: LineSegment StartX=39 StartY=150 StartZ=0 EndX=95 EndY=150 EndZ=0
    g7: LineSegment StartX=-39 StartY=150 StartZ=0 EndX=-95 EndY=150 EndZ=0
    g8: LineSegment StartX=-53.2008 StartY=106 StartZ=0 EndX=-21.2008 EndY=106 EndZ=0
    g9: LineSegment StartX=-21.2008 StartY=106 StartZ=0 EndX=-21.2008 EndY=42 EndZ=0
    g10: LineSegment StartX=-21.2008 StartY=42 StartZ=0 EndX=-53.2008 EndY=42 EndZ=0
    g11: LineSegment StartX=-53.2008 StartY=42 StartZ=0 EndX=-53.2008 EndY=106 EndZ=0
    g12: LineSegment StartX=21.2008 StartY=106 StartZ=0 EndX=21.2008 EndY=42 EndZ=0
    g13: LineSegment StartX=53.2008 StartY=106 StartZ=0 EndX=21.2008 EndY=106 EndZ=0
    g14: LineSegment StartX=53.2008 StartY=42 StartZ=0 EndX=53.2008 EndY=106 EndZ=0
    g15: LineSegment StartX=21.2008 StartY=42 StartZ=0 EndX=53.2008 EndY=42 EndZ=0
  constraints (43):
    c: Coincident(g0,g1)
    c: Coincident(g2,g0)
    c: Horizontal(g0)
    c: Vertical(g1)
    c: Vertical(g2)
    c: PointOnObject(g0,g-1)
    c: Symmetric(g0,g0,g-2)
    c: DistanceX(g0,g0) = 190
    c: DistanceY(g1,g1) = 150
    c: Coincident(g3,g4)
    c: Coincident(g4,g5)
    c: Horizontal(g4)
    c: Vertical(g3)
    c: Vertical(g5)
    c: Coincident(g6,g3)
    c: Coincident(g6,g1)
    c: Coincident(g7,g2)
    c: Coincident(g5,g7)
    c: Horizontal(g7)
    c: DistanceY(g2,g2) = 150
    c: Horizontal(g6)
    c: Equal(g6,g7)
    c: DistanceX(g4,g4) = 78
    c: Coincident(g8,g9)
    c: Coincident(g9,g10)
    c: Coincident(g10,g11)
    c: Coincident(g11,g8)
    c: Horizontal(g8)
    c: Horizontal(g10)
    c: Vertical(g9)
    c: Vertical(g11)
    c: DistanceX(g8,g8) = 32
    c: DistanceY(g11,g11) = 64
    c: DistanceY(g-1,g10) = 42
    c: DistanceY(g5,g5) = 39
    c: Coincident(g13,g12)
    c: Coincident(g12,g15)
    c: Coincident(g15,g14)
    c: Coincident(g14,g13)
    c: Horizontal(g13)
    c: Horizontal(g15)
    c: Vertical(g12)
    c: Vertical(g14)
FEATURE [PartDesign::Pad] Pad015  label="Avant tete001"
  Length = 18
  Length2 = 100
  Placement = pos=(0,0,0) rot=(0.57735,0.57735,0.57735;2.0944rad)
  Profile = -> Sketch047
  Type = 0
FEATURE [Sketcher::SketchObject] Sketch048  label="RaspberryPi002"
  AttachmentOffset = pos=(21,0,185) rot=(0,1,0;-0.680678rad)
  MapMode = 5
  Placement = pos=(21,0,185) rot=(0,1,0;5.60251rad)
  Support = -> [XY_Plane019]
  sketch-geometry (5):
    g0: LineSegment StartX=21.1908 StartY=76.9941 StartZ=0 EndX=91.1908 EndY=76.9941 EndZ=0
    g1: LineSegment StartX=91.1907 StartY=-77.0059 StartZ=0 EndX=21.1908 EndY=-77.0059 EndZ=0
    g2: LineSegment StartX=21.1908 StartY=-77.0059 StartZ=0 EndX=21.1908 EndY=76.9941 EndZ=0
    g3: ArcOfCircle CenterX=91.1909 CenterY=-47.0059 CenterZ=0 NormalX=0 NormalY=0 NormalZ=1 AngleXU=0 Radius=30 StartAngle=4.71238 EndAngle=7.85398
    g4: LineSegment StartX=91.1908 StartY=-17.0059 StartZ=0 EndX=91.1908 EndY=76.9941 EndZ=0
  constraints (12):
    c: Coincident(g1,g2)
    c: Coincident(g2,g0)
    c: Horizontal(g0)
    c: Horizontal(g1)
    c: Vertical(g2)
    c: DistanceY(g1,g0) = 154
    c: DistanceX(g0,g0) = 70
    c: Radius(g3) = 30
    c: Coincident(g3,g1)
    c: Coincident(g4,g3)
    c: Coincident(g4,g0)
    c: Vertical(g4)
FEATURE [PartDesign::Pad] Pad016  label="RaspberryPi001"
  Length = 35
  Length2 = 100
  Profile = -> Sketch048
  Type = 0
FEATURE [PartDesign::Body] Body017  label="RaspberryPi"
  Group = -> [Sketch048,Pad016]
  Origin = -> Origin019
  Tip = -> Pad016
FEATURE [App::DocumentObjectGroup] Groupe  label="Electronique"
  Group = -> [Part__Mirroring003,Box008,Box009,Box010,Cylinder003,Box011,Body006,CloneBody,Body007,Body017]
FEATURE [TechDraw::DrawSVGTemplate] Template001
  Height = 210
  Orientation = 1
  Width = 297
FEATURE [TechDraw::DrawProjGroupItem] ProjItem  label="Front"
  CoarseView = false
  Direction = (-1,0,0)
  Focus = 100
  HardHidden = false
  IsoCount = 0
  IsoHidden = false
  IsoVisible = false
  LockPosition = false
  Perspective = false
  Rotation = 0
  RotationVector = (0,1,0)
  ScaleType = 0
  SeamHidden = false
  SeamVisible = false
  SmoothHidden = false
  SmoothVisible = false
  Source = -> [Sketch002]
  Type = 0
  X = 0
  Y = 0
FEATURE [TechDraw::DrawProjGroup] ProjGroup
  Anchor = -> ProjItem
  AutoDistribute = true
  CubeDirs = (6) [(0,0,-1),(-1,-6.12323e-17,0),(-6.12323e-17,1,0),(1,6.12323e-17,0),(6.12323e-17,-1,0),(0,0,1)]
  CubeRotations = (6) [(6.12323e-17,1,0),(6.12323e-17,1,0),(-1,6.12323e-17,0),(-6.12323e-17,-1,0),(1,-6.12323e-17,0),(6.12323e-17,1,0)]
  LockPosition = false
  ProjectionType = 0
  Rotation = 0
  ScaleType = 0
  Source = -> [Sketch002]
  Views = -> [ProjItem]
  X = 148.5
  Y = 105
  spacingX = 15
  spacingY = 15
FEATURE [TechDraw::DrawViewDimension] Dimension
  FormatSpec = %.2f
  LockPosition = false
  MeasureType = 1
  References2D = -> [ProjItem]
  Rotation = 0
  ScaleType = 0
  Type = 1
  X = -1.56716
  Y = 82.7985
FEATURE [TechDraw::DrawViewDimension] Dimension001
  FormatSpec = %.2f
  LockPosition = false
  MeasureType = 1
  References2D = -> [ProjItem]
  Rotation = 0
  ScaleType = 0
  Type = 2
  X = -142.525
  Y = 1.39304
FEATURE [TechDraw::DrawViewDimension] Dimension002
  FormatSpec = %.2f
  LockPosition = false
  MeasureType = 1
  References2D = -> [ProjItem]
  Rotation = 0
  ScaleType = 0
  Type = 2
  X = 0
  Y = 0
FEATURE [TechDraw::DrawViewDimension] Dimension003
  FormatSpec = %.2f
  LockPosition = false
  MeasureType = 1
  References2D = -> [ProjItem]
  Rotation = 0
  ScaleType = 0
  Type = 2
  X = 16.107
  Y = -0.087065
FEATURE [TechDraw::DrawViewDimension] Dimension004
  FormatSpec = %.2f
  LockPosition = false
  MeasureType = 1
  References2D = -> [ProjItem]
  Rotation = 0
  ScaleType = 0
  Type = 1
  X = -0.261194
  Y = 17.9353
FEATURE [TechDraw::DrawProjGroupItem] ProjItem001  label="Front001"
  CoarseView = false
  Direction = (-1,0,0)
  Focus = 100
  HardHidden = false
  IsoCount = 0
  IsoHidden = false
  IsoVisible = false
  LockPosition = false
  Perspective = false
  Rotation = 0
  RotationVector = (0,1,0)
  ScaleType = 0
  SeamHidden = false
  SeamVisible = false
  SmoothHidden = false
  SmoothVisible = false
  Source = -> [Sketch042]
  Type = 0
  X = 0
  Y = 0
FEATURE [TechDraw::DrawProjGroup] ProjGroup001
  Anchor = -> ProjItem001
  AutoDistribute = true
  CubeDirs = (6) [(0,0,-1),(-1,-6.12323e-17,0),(-6.12323e-17,1,0),(1,6.12323e-17,0),(6.12323e-17,-1,0),(0,0,1)]
  CubeRotations = (6) [(6.12323e-17,1,0),(6.12323e-17,1,0),(-1,6.12323e-17,0),(-6.12323e-17,-1,0),(1,-6.12323e-17,0),(6.12323e-17,1,0)]
  LockPosition = false
  ProjectionType = 0
  Rotation = 0
  ScaleType = 0
  Source = -> [Sketch042]
  Views = -> [ProjItem001]
  X = 148.5
  Y = 105
  spacingX = 15
  spacingY = 15
FEATURE [TechDraw::DrawViewDimension] Dimension005
  FormatSpec = %.2f
  LockPosition = false
  MeasureType = 1
  References2D = -> [ProjItem001]
  Rotation = 0
  ScaleType = 0
  Type = 2
  X = -144.614
  Y = 6.35572
FEATURE [TechDraw::DrawViewDimension] Dimension006
  FormatSpec = %.2f
  LockPosition = false
  MeasureType = 1
  References2D = -> [ProjItem001]
  Rotation = 0
  ScaleType = 0
  Type = 1
  X = -8.35821
  Y = 83.9303
FEATURE [TechDraw::DrawViewDimension] Dimension007
  FormatSpec = %.2f
  LockPosition = false
  MeasureType = 1
  References2D = -> [ProjItem001]
  Rotation = 0
  ScaleType = 0
  Type = 1
  X = -2.17662
  Y = -45.4478
FEATURE [TechDraw::DrawViewDimension] Dimension008
  FormatSpec = %.2f
  LockPosition = false
  MeasureType = 1
  References2D = -> [ProjItem001]
  Rotation = 0
  ScaleType = 0
  Type = 2
  X = -105.958
  Y = 1.82836
FEATURE [TechDraw::DrawProjGroupItem] ProjItem002  label="Front002"
  CoarseView = false
  Direction = (0,0,1)
  Focus = 100
  HardHidden = false
  IsoCount = 0
  IsoHidden = false
  IsoVisible = false
  LockPosition = false
  Perspective = false
  Rotation = 0
  RotationVector = (0,1,0)
  ScaleType = 0
  SeamHidden = false
  SeamVisible = false
  SmoothHidden = false
  SmoothVisible = false
  Source = -> [Pad013]
  Type = 0
  X = 0
  Y = 0
FEATURE [TechDraw::DrawProjGroup] ProjGroup002
  Anchor = -> ProjItem002
  AutoDistribute = true
  CubeDirs = (6) [(-1,-6.12323e-17,-6.12323e-17),(-6.12323e-17,-3.7494e-33,1),(-6.12323e-17,1,0),(6.12323e-17,3.7494e-33,-1),(6.12323e-17,-1,0),(1,6.12323e-17,6.12323e-17)]
  CubeRotations = (6) [(6.12323e-17,1,0),(6.12323e-17,1,0),(6.12323e-17,-1.22465e-16,1),(-6.12323e-17,-1,0),(-6.12323e-17,1.22465e-16,-1),(6.12323e-17,1,0)]
  LockPosition = false
  ProjectionType = 0
  Rotation = 0
  ScaleType = 0
  Source = -> [Pad013]
  Views = -> [ProjItem002]
  X = 148.5
  Y = 105
  spacingX = 15
  spacingY = 15
FEATURE [TechDraw::DrawViewDimension] Dimension009
  FormatSpec = %.2f
  LockPosition = false
  MeasureType = 1
  References2D = -> [ProjItem002]
  Rotation = 0
  ScaleType = 0
  Type = 1
  X = -7.05224
  Y = 67.9975
FEATURE [TechDraw::DrawViewDimension] Dimension010
  FormatSpec = %.2f
  LockPosition = false
  MeasureType = 1
  References2D = -> [ProjItem002]
  Rotation = 0
  ScaleType = 0
  Type = 2
  X = -113.532
  Y = -0.174129
FEATURE [TechDraw::DrawProjGroupItem] ProjItem003  label="Front003"
  CoarseView = false
  Direction = (0,0,1)
  Focus = 100
  HardHidden = false
  IsoCount = 0
  IsoHidden = false
  IsoVisible = false
  LockPosition = false
  Perspective = false
  Rotation = 0
  RotationVector = (0,-1,0)
  ScaleType = 0
  SeamHidden = false
  SeamVisible = false
  SmoothHidden = false
  SmoothVisible = false
  Source = -> [Pad]
  Type = 0
  X = 0
  Y = 0
FEATURE [TechDraw::DrawProjGroup] ProjGroup003
  Anchor = -> ProjItem003
  AutoDistribute = true
  CubeDirs = (6) [(1,-6.12323e-17,-3.7494e-33),(0,-6.12323e-17,1),(-6.12323e-17,-1,-6.12323e-17),(0,6.12323e-17,-1),(6.12323e-17,1,6.12323e-17),(-1,6.12323e-17,3.7494e-33)]
  CubeRotations = (6) [(6.12323e-17,-1,-6.12323e-17),(6.12323e-17,-1,-6.12323e-17),(0,6.12323e-17,1),(-6.12323e-17,1,6.12323e-17),(0,-6.12323e-17,-1),(6.12323e-17,-1,-6.12323e-17)]
  LockPosition = false
  ProjectionType = 0
  Rotation = 0
  ScaleType = 0
  Source = -> [Pad]
  Views = -> [ProjItem003]
  X = 148.5
  Y = 105
  spacingX = 15
  spacingY = 15
FEATURE [TechDraw::DrawProjGroupItem] ProjItem004  label="Front004"
  CoarseView = false
  Direction = (-1,0,0)
  Focus = 100
  HardHidden = false
  IsoCount = 0
  IsoHidden = false
  IsoVisible = false
  LockPosition = false
  Perspective = false
  Rotation = 0
  RotationVector = (0,1,0)
  ScaleType = 0
  SeamHidden = false
  SeamVisible = false
  SmoothHidden = false
  SmoothVisible = false
  Source = -> [Sketch047]
  Type = 0
  X = 0
  Y = 0
FEATURE [TechDraw::DrawProjGroup] ProjGroup004
  Anchor = -> ProjItem004
  AutoDistribute = true
  CubeDirs = (6) [(0,0,-1),(-1,-6.12323e-17,0),(-6.12323e-17,1,0),(1,6.12323e-17,0),(6.12323e-17,-1,0),(0,0,1)]
  CubeRotations = (6) [(6.12323e-17,1,0),(6.12323e-17,1,0),(-1,6.12323e-17,0),(-6.12323e-17,-1,0),(1,-6.12323e-17,0),(6.12323e-17,1,0)]
  LockPosition = false
  ProjectionType = 0
  Rotation = 0
  ScaleType = 0
  Source = -> [Sketch047]
  Views = -> [ProjItem004]
  X = 148.5
  Y = 105
  spacingX = 15
  spacingY = 15
FEATURE [TechDraw::DrawViewDimension] Dimension011
  FormatSpec = %.2f
  LockPosition = false
  MeasureType = 1
  References2D = -> [ProjItem004]
  Rotation = 0
  ScaleType = 0
  Type = 1
  X = -2.00249
  Y = -51.7164
FEATURE [TechDraw::DrawViewDimension] Dimension012
  FormatSpec = %.2f
  LockPosition = false
  MeasureType = 1
  References2D = -> [ProjItem004]
  Rotation = 0
  ScaleType = 0
  Type = 2
  X = -81.9279
  Y = -0.609453
FEATURE [TechDraw::DrawProjGroupItem] ProjItem005  label="Front005"
  CoarseView = false
  Direction = (0,0,-1)
  Focus = 100
  HardHidden = false
  IsoCount = 0
  IsoHidden = false
  IsoVisible = false
  LockPosition = false
  Perspective = false
  Rotation = 0
  RotationVector = (0,1,0)
  ScaleType = 0
  SeamHidden = false
  SeamVisible = false
  SmoothHidden = false
  SmoothVisible = false
  Source = -> [Fillet003]
  Type = 0
  X = 0
  Y = 0
FEATURE [TechDraw::DrawProjGroup] ProjGroup005
  Anchor = -> ProjItem005
  AutoDistribute = true
  CubeDirs = (6) [(1,6.12323e-17,-6.12323e-17),(-6.12323e-17,-3.7494e-33,-1),(-6.12323e-17,1,0),(6.12323e-17,3.7494e-33,1),(6.12323e-17,-1,0),(-1,-6.12323e-17,6.12323e-17)]
  CubeRotations = (6) [(6.12323e-17,1,0),(6.12323e-17,1,0),(6.12323e-17,-1.22465e-16,-1),(-6.12323e-17,-1,0),(-6.12323e-17,1.22465e-16,1),(6.12323e-17,1,0)]
  LockPosition = false
  ProjectionType = 0
  Rotation = 0
  ScaleType = 0
  Source = -> [Fillet003]
  Views = -> [ProjItem005]
  X = 148.5
  Y = 105
  spacingX = 15
  spacingY = 15
FEATURE [TechDraw::DrawViewDimension] Dimension013
  FormatSpec = %.2f
  LockPosition = false
  MeasureType = 1
  References2D = -> [ProjItem005]
  Rotation = 0
  ScaleType = 0
  Type = 1
  X = -0.522388
  Y = 69.3905
FEATURE [TechDraw::DrawViewDimension] Dimension014
  FormatSpec = %.2f
  LockPosition = false
  MeasureType = 1
  References2D = -> [ProjItem005]
  Rotation = 0
  ScaleType = 0
  Type = 2
  X = 86.3682
  Y = 0.522388
FEATURE [Sketcher::SketchObject] Sketch049  label="Cote tete002"
  AttachmentOffset = pos=(0,190,95) rot=(0,0,1;0rad)
  MapMode = 5
  Placement = pos=(0,-95,190) rot=(1,0,0;1.5708rad)
  Support = -> [XZ_Plane020]
  sketch-geometry (5):
    g0: ArcOfCircle CenterX=73.3704 CenterY=80 CenterZ=0 NormalX=0 NormalY=0 NormalZ=1 AngleXU=0 Radius=72.3704 StartAngle=1.82744 EndAngle=3.14159
    g1: LineSegment StartX=1 StartY=0 StartZ=0 EndX=107 EndY=0 EndZ=0
    g2: LineSegment StartX=107 StartY=0 StartZ=0 EndX=107 EndY=150 EndZ=0
    g3: LineSegment StartX=107 StartY=150 StartZ=0 EndX=55 EndY=150 EndZ=0
    g4: LineSegment StartX=1 StartY=80 StartZ=0 EndX=1 EndY=0 EndZ=0
  constraints (16):
    c: Horizontal(g1)
    c: Vertical(g2)
    c: Coincident(g3,g2)
    c: Coincident(g4,g0)
    c: Coincident(g4,g1)
    c: Vertical(g4)
    c: DistanceX(g-1,g1) = 1
    c: PointOnObject(g1,g-1)
    c: DistanceX(g1,g1) = 106
    c: Coincident(g2,g1)
    c: Coincident(g3,g0)
    c: DistanceY(g2,g2) = 150
    c: Horizontal(g3)
    c: DistanceX(g3,g3) = 52
    c: DistanceY(g4,g4) = 80
    c: DistanceY(g0) = 80
FEATURE [PartDesign::Pad] Pad017  label="Cote tete001"
  Length = 18
  Length2 = 100
  Placement = pos=(0,0,0) rot=(1,0,0;1.5708rad)
  Profile = -> Sketch049
  Reversed = true
  Type = 0
FEATURE [TechDraw::DrawProjGroupItem] ProjItem006  label="Front006"
  CoarseView = false
  Direction = (0,-1,0)
  Focus = 100
  HardHidden = false
  IsoCount = 0
  IsoHidden = false
  IsoVisible = false
  LockPosition = false
  Perspective = false
  Rotation = 0
  RotationVector = (1,0,0)
  ScaleType = 0
  SeamHidden = false
  SeamVisible = false
  SmoothHidden = false
  SmoothVisible = false
  Source = -> [Pad017]
  Type = 0
  X = 0
  Y = 0
FEATURE [TechDraw::DrawProjGroup] ProjGroup006
  Anchor = -> ProjItem006
  AutoDistribute = true
  CubeDirs = (1) [(0,0,0)]
  CubeRotations = (1) [(0,0,0)]
  LockPosition = false
  ProjectionType = 0
  Rotation = 0
  ScaleType = 0
  Source = -> [Pad017]
  Views = -> [ProjItem006]
  X = 148.5
  Y = 105
  spacingX = 15
  spacingY = 15
FEATURE [TechDraw::DrawViewDimension] Dimension015
  FormatSpec = %.2f
  LockPosition = false
  MeasureType = 1
  References2D = -> [ProjItem006]
  Rotation = 0
  ScaleType = 0
  Type = 1
  X = 0
  Y = -27.1642
FEATURE [TechDraw::DrawViewDimension] Dimension016
  FormatSpec = %.2f
  LockPosition = false
  MeasureType = 1
  References2D = -> [ProjItem006]
  Rotation = 0
  ScaleType = 0
  Type = 2
  X = 14.9751
  Y = -0.261194
FEATURE [TechDraw::DrawProjGroupItem] ProjItem007  label="Front007"
  CoarseView = false
  Direction = (0,0,-1)
  Focus = 100
  HardHidden = false
  IsoCount = 0
  IsoHidden = false
  IsoVisible = false
  LockPosition = false
  Perspective = false
  Rotation = 0
  RotationVector = (0,1,0)
  ScaleType = 0
  SeamHidden = false
  SeamVisible = false
  SmoothHidden = false
  SmoothVisible = false
  Source = -> [Pad014]
  Type = 0
  X = 0
  Y = 0
FEATURE [TechDraw::DrawProjGroup] ProjGroup007
  Anchor = -> ProjItem007
  AutoDistribute = true
  CubeDirs = (6) [(1,6.12323e-17,-6.12323e-17),(-6.12323e-17,-3.7494e-33,-1),(-6.12323e-17,1,0),(6.12323e-17,3.7494e-33,1),(6.12323e-17,-1,0),(-1,-6.12323e-17,6.12323e-17)]
  CubeRotations = (6) [(6.12323e-17,1,0),(6.12323e-17,1,0),(6.12323e-17,-1.22465e-16,-1),(-6.12323e-17,-1,0),(-6.12323e-17,1.22465e-16,1),(6.12323e-17,1,0)]
  LockPosition = false
  ProjectionType = 0
  Rotation = 0
  ScaleType = 0
  Source = -> [Pad014]
  Views = -> [ProjItem007]
  X = 148.5
  Y = 105
  spacingX = 15
  spacingY = 15
FEATURE [TechDraw::DrawViewDimension] Dimension017
  FormatSpec = %.2f
  LockPosition = false
  MeasureType = 1
  References2D = -> [ProjItem007]
  Rotation = 0
  ScaleType = 0
  Type = 1
  X = 52.7612
  Y = -39.6144
FEATURE [TechDraw::DrawViewDimension] Dimension018
  FormatSpec = %.2f
  LockPosition = false
  MeasureType = 1
  References2D = -> [ProjItem007]
  Rotation = 0
  ScaleType = 0
  Type = 2
  X = -57.4627
  Y = 17.5
FEATURE [Sketcher::SketchObject] Sketch050  label="Derriere tete002"
  AttachmentOffset = pos=(0,190,0) rot=(0,0,1;0rad)
  MapMode = 5
  Placement = pos=(0,-2e-11,190) rot=(1,0,0;1.5708rad)
  Support = -> [XZ_Plane021]
  sketch-geometry (4):
    g0: LineSegment StartX=1 StartY=18 StartZ=0 EndX=19 EndY=18 EndZ=0
    g1: LineSegment StartX=19 StartY=18 StartZ=0 EndX=19 EndY=48 EndZ=0
    g2: LineSegment StartX=19 StartY=48 StartZ=0 EndX=1 EndY=48 EndZ=0
    g3: LineSegment StartX=1 StartY=48 StartZ=0 EndX=1 EndY=18 EndZ=0
  constraints (12):
    c: Coincident(g0,g1)
    c: Coincident(g1,g2)
    c: Coincident(g2,g3)
    c: Coincident(g3,g0)
    c: Horizontal(g0)
    c: Horizontal(g2)
    c: Vertical(g1)
    c: Vertical(g3)
    c: DistanceX(g2,g2) = 18
    c: DistanceX(g-1,g0) = 1
    c: DistanceY(g-1,g0) = 18
    c: DistanceY(g3,g3) = 30
FEATURE [PartDesign::Pad] Pad018  label="Derriere tete001"
  Length = 154
  Length2 = 100
  Midplane = true
  Placement = pos=(0,0,0) rot=(1,0,0;1.5708rad)
  Profile = -> Sketch050
  Type = 0
FEATURE [PartDesign::Body] Body019  label="Derriere tete"
  Group = -> [Sketch050,Pad018]
  Origin = -> Origin021
  Tip = -> Pad018
FEATURE [TechDraw::DrawProjGroupItem] ProjItem008  label="Front008"
  CoarseView = false
  Direction = (-1,0,0)
  Focus = 100
  HardHidden = false
  IsoCount = 0
  IsoHidden = false
  IsoVisible = false
  LockPosition = false
  Perspective = false
  Rotation = 0
  RotationVector = (0,1,0)
  ScaleType = 0
  SeamHidden = false
  SeamVisible = false
  SmoothHidden = false
  SmoothVisible = false
  Source = -> [Pad018]
  Type = 0
  X = 0
  Y = 0
FEATURE [TechDraw::DrawProjGroup] ProjGroup008
  Anchor = -> ProjItem008
  AutoDistribute = true
  CubeDirs = (6) [(0,0,-1),(-1,-6.12323e-17,0),(-6.12323e-17,1,0),(1,6.12323e-17,0),(6.12323e-17,-1,0),(0,0,1)]
  CubeRotations = (6) [(6.12323e-17,1,0),(6.12323e-17,1,0),(-1,6.12323e-17,0),(-6.12323e-17,-1,0),(1,-6.12323e-17,0),(6.12323e-17,1,0)]
  LockPosition = false
  ProjectionType = 0
  Rotation = 0
  ScaleType = 0
  Source = -> [Pad018]
  Views = -> [ProjItem008]
  X = 148.5
  Y = 105
  spacingX = 15
  spacingY = 15
FEATURE [TechDraw::DrawViewDimension] Dimension019
  FormatSpec = %.2f
  LockPosition = false
  MeasureType = 1
  References2D = -> [ProjItem008]
  Rotation = 0
  ScaleType = 0
  Type = 1
  X = 0
  Y = 0
FEATURE [TechDraw::DrawViewDimension] Dimension020
  FormatSpec = %.2f
  LockPosition = false
  MeasureType = 1
  References2D = -> [ProjItem008]
  Rotation = 0
  ScaleType = 0
  Type = 2
  X = -63.5572
  Y = -0.957711
FEATURE [TechDraw::DrawPage] Page002  label="Impressions"
  KeepUpdated = true
  ProjectionType = 0
  Template = -> Template001
  Views = -> [ProjGroup,Dimension,Dimension001,Dimension002,Dimension003,Dimension004,ProjGroup001,Dimension005,Dimension006,Dimension007,Dimension008,ProjGroup002,Dimension009,Dimension010,ProjGroup003,ProjGroup004,Dimension011,Dimension012,ProjGroup005,Dimension013,Dimension014,ProjGroup006,Dimension015,Dimension016,ProjGroup007,Dimension017,Dimension018,ProjGroup008,Dimension019,Dimension020]
FEATURE [PartDesign::Fillet] Fillet  label="Fillet face avant"
  Base = -> Pad002 [Edge4,Edge10]
  BaseFeature = -> Pad002
  Placement = pos=(132,0,0) rot=(0.57735,0.57735,0.57735;2.0944rad)
  Radius = 5
FEATURE [Sketcher::SketchObject] Sketch  label="Cavite roue"
  MapMode = 5
  Placement = pos=(0,0,0) rot=(0.57735,0.57735,0.57735;2.0944rad)
  Support = -> [YZ_Plane003]
  sketch-geometry (8):
    g0: LineSegment StartX=-106 StartY=0 StartZ=0 EndX=-88 EndY=0 EndZ=0
    g1: LineSegment StartX=-88 StartY=0 StartZ=0 EndX=-88 EndY=70 EndZ=0
    g2: LineSegment StartX=-88 StartY=70 StartZ=0 EndX=-106 EndY=70 EndZ=0
    g3: LineSegment StartX=-106 StartY=70 StartZ=0 EndX=-106 EndY=0 EndZ=0
    g4: LineSegment StartX=106 StartY=0 StartZ=0 EndX=88 EndY=0 EndZ=0
    g5: LineSegment StartX=88 StartY=0 StartZ=0 EndX=88 EndY=70 EndZ=0
    g6: LineSegment StartX=88 StartY=70 StartZ=0 EndX=106 EndY=70 EndZ=0
    g7: LineSegment StartX=106 StartY=70 StartZ=0 EndX=106 EndY=0 EndZ=0
  constraints (23):
    c: Coincident(g0,g1)
    c: Coincident(g1,g2)
    c: Coincident(g2,g3)
    c: Coincident(g3,g0)
    c: Horizontal(g0)
    c: Horizontal(g2)
    c: Vertical(g1)
    c: Vertical(g3)
    c: Coincident(g4,g5)
    c: Coincident(g5,g6)
    c: Coincident(g6,g7)
    c: Coincident(g7,g4)
    c: Horizontal(g4)
    c: Horizontal(g6)
    c: Vertical(g5)
    c: Vertical(g7)
    c: Symmetric(g1,g5,g-2)
    c: DistanceY(g5,g5) = 70
    c: DistanceX(g6,g6) = 18
    c: Equal(g1,g5)
    c: Equal(g2,g6)
    c: DistanceX(g-1,g4) = 106
    c: DistanceY(g-1,g4) = 0
FEATURE [PartDesign::Pocket] Pocket
  BaseFeature = -> Fillet
  Length = 145
  Length2 = 100
  Placement = pos=(132,0,0) rot=(0.57735,0.57735,0.57735;2.0944rad)
  Profile = -> Sketch
  Reversed = true
  Type = 0
FEATURE [PartDesign::Body] Body003  label="Face avant"
  Group = -> [Sketch002,Pad002,Fillet,Sketch,Pocket]
  Origin = -> Origin003
  Tip = -> Pocket
FEATURE [PartDesign::Fillet] Fillet008  label="Fillet face arriere"
  Base = -> Pad011 [Edge15,Edge9]
  BaseFeature = -> Pad011
  Placement = pos=(0,0,0) rot=(0.57735,0.57735,0.57735;2.0944rad)
  Radius = 5
FEATURE [PartDesign::Body] Body010  label="Face arriere"
  Group = -> [Sketch042,Pad011,Fillet008]
  Origin = -> Origin012
  Tip = -> Fillet008
FEATURE [PartDesign::Fillet] Fillet009
  Base = -> Pad014 [Edge11]
  BaseFeature = -> Pad014
  Radius = 5
FEATURE [PartDesign::Body] Body014  label="Dessous tete"
  Group = -> [Sketch046,Pad014,Fillet009]
  Origin = -> Origin016
  Tip = -> Fillet009
FEATURE [PartDesign::Fillet] Fillet010  label="Fillet avant tete"
  Base = -> Pad015 [Edge7,Edge1,Edge2,Edge4,Edge24]
  BaseFeature = -> Pad015
  Placement = pos=(0,0,0) rot=(0.57735,0.57735,0.57735;2.0944rad)
  Radius = 5
FEATURE [PartDesign::Body] Body015  label="Avant tete"
  Group = -> [Sketch047,Pad015,Fillet010]
  Origin = -> Origin017
  Tip = -> Fillet010
FEATURE [PartDesign::Fillet] Fillet011  label="Fillet cote tete"
  Base = -> Pad017 [Edge9,Edge5]
  BaseFeature = -> Pad017
  Placement = pos=(0,0,0) rot=(1,0,0;1.5708rad)
  Radius = 5
FEATURE [PartDesign::Body] Body018  label="Cote tete"
  Group = -> [Sketch049,Pad017,Fillet011]
  Origin = -> Origin020
  Tip = -> Fillet011
FEATURE [PartDesign::FeatureBase] Clone001  label="Oreille001"
  BaseFeature = -> Cylinder002
  Placement = pos=(76,-95,290) rot=(1,0,0;1.5708rad)
FEATURE [PartDesign::FeatureBase] Clone002  label="Oeil001"
  BaseFeature = -> Box005
  Placement = pos=(103,22,232) rot=(0,0,1;0rad)
FEATURE [PartDesign::FeatureBase] Clone004  label="Roue"
  BaseFeature = -> Cylinder004
  Placement = pos=(105,104,37.5) rot=(1,0,0;1.5708rad)
FEATURE [Sketcher::SketchObject] Sketch051  label="Cote tete003"
  AttachmentOffset = pos=(0,190,-95) rot=(0,0,1;0rad)
  MapMode = 5
  Placement = pos=(0,95,190) rot=(1,0,0;1.5708rad)
  Support = -> [XZ_Plane022]
  sketch-geometry (5):
    g0: ArcOfCircle CenterX=73.3704 CenterY=80 CenterZ=0 NormalX=0 NormalY=0 NormalZ=1 AngleXU=0 Radius=72.3704 StartAngle=1.82744 EndAngle=3.14159
    g1: LineSegment StartX=1 StartY=0 StartZ=0 EndX=107 EndY=0 EndZ=0
    g2: LineSegment StartX=107 StartY=0 StartZ=0 EndX=107 EndY=150 EndZ=0
    g3: LineSegment StartX=107 StartY=150 StartZ=0 EndX=55 EndY=150 EndZ=0
    g4: LineSegment StartX=1 StartY=80 StartZ=0 EndX=1 EndY=0 EndZ=0
  constraints (16):
    c: Horizontal(g1)
    c: Vertical(g2)
    c: Coincident(g3,g2)
    c: Coincident(g4,g0)
    c: Coincident(g4,g1)
    c: Vertical(g4)
    c: DistanceX(g-1,g1) = 1
    c: PointOnObject(g1,g-1)
    c: DistanceX(g1,g1) = 106
    c: Coincident(g2,g1)
    c: Coincident(g3,g0)
    c: DistanceY(g2,g2) = 150
    c: Horizontal(g3)
    c: DistanceX(g3,g3) = 52
    c: DistanceY(g4,g4) = 80
    c: DistanceY(g0) = 80
FEATURE [PartDesign::Pad] Pad019  label="Cote tete004"
  Length = 18
  Length2 = 100
  Placement = pos=(0,0,0) rot=(1,0,0;1.5708rad)
  Profile = -> Sketch051
  Type = 0
FEATURE [PartDesign::Fillet] Fillet012  label="Fillet cote tete001"
  Base = -> Pad019 [Edge9,Edge5]
  BaseFeature = -> Pad019
  Placement = pos=(0,0,0) rot=(1,0,0;1.5708rad)
  Radius = 5
FEATURE [PartDesign::Body] Body020  label="Cote tete005"
  Group = -> [Sketch051,Pad019,Fillet012]
  Origin = -> Origin022
  Tip = -> Fillet012
FEATURE [Sketcher::SketchObject] Sketch052
  AttachmentOffset = pos=(0,0,-125) rot=(0,0,1;0rad)
  MapMode = 5
  Placement = pos=(0,125,1.3e-11) rot=(1,0,0;1.5708rad)
  Support = -> [XZ_Plane023]
  sketch-geometry (4):
    g0: LineSegment StartX=18 StartY=10 StartZ=0 EndX=132 EndY=10 EndZ=0
    g1: LineSegment StartX=132 StartY=10 StartZ=0 EndX=132 EndY=142 EndZ=0
    g2: LineSegment StartX=132 StartY=142 StartZ=0 EndX=18 EndY=142 EndZ=0
    g3: LineSegment StartX=18 StartY=142 StartZ=0 EndX=18 EndY=10 EndZ=0
  constraints (12):
    c: Coincident(g0,g1)
    c: Coincident(g1,g2)
    c: Coincident(g2,g3)
    c: Coincident(g3,g0)
    c: Horizontal(g0)
    c: Horizontal(g2)
    c: Vertical(g1)
    c: Vertical(g3)
    c: DistanceY(g3,g3) = 132
    c: DistanceY(g-1,g0) = 10
    c: DistanceX(g-1,g0) = 18
    c: DistanceX(g0,g0) = 114
FEATURE [Sketcher::SketchObject] Sketch053
  AttachmentOffset = pos=(0,0,-125) rot=(0,0,1;0rad)
  MapMode = 5
  Placement = pos=(0,125,1.3e-11) rot=(1,0,0;1.5708rad)
  Support = -> [XZ_Plane023]
  expr: Constraints[6] = 75 / 2
  expr: Constraints[8] = 45 - 18
  expr: Constraints[10] = 46 / 2
  sketch-geometry (15):
    g0: LineSegment StartX=18 StartY=10 StartZ=0 EndX=132 EndY=10 EndZ=0
    g1: LineSegment StartX=132 StartY=10 StartZ=0 EndX=132 EndY=142 EndZ=0
    g2: Circle [constr] CenterX=105 CenterY=37.5 CenterZ=0 NormalX=0 NormalY=0 NormalZ=1 AngleXU=0 Radius=37.5
    g3: Circle [constr] CenterX=105 CenterY=37.5 CenterZ=0 NormalX=0 NormalY=0 NormalZ=1 AngleXU=0 Radius=23
    g4: LineSegment StartX=105 StartY=60.5 StartZ=0 EndX=27 EndY=60.5 EndZ=0
    g5: ArcOfCircle CenterX=105 CenterY=37.5 CenterZ=0 NormalX=0 NormalY=0 NormalZ=1 AngleXU=0 Radius=23 StartAngle=4.54308 EndAngle=7.85398
    g6: LineSegment [constr] StartX=105 StartY=60.5 StartZ=0 EndX=105 EndY=37.5 EndZ=0
    g7: LineSegment StartX=27 StartY=60.5 StartZ=0 EndX=27 EndY=27.5 EndZ=0
    g8: LineSegment StartX=27 StartY=27.5 StartZ=0 EndX=101.125 EndY=14.8289 EndZ=0
    g9: LineSegment StartX=28 StartY=142 StartZ=0 EndX=28 EndY=80.5 EndZ=0
    g10: LineSegment StartX=28 StartY=80.5 StartZ=0 EndX=97 EndY=80.5 EndZ=0
    g11: LineSegment StartX=97 StartY=80.5 StartZ=0 EndX=97 EndY=142 EndZ=0
    g12: LineSegment StartX=18 StartY=142 StartZ=0 EndX=18 EndY=10 EndZ=0
    g13: LineSegment StartX=18 StartY=142 StartZ=0 EndX=28 EndY=142 EndZ=0
    g14: LineSegment StartX=97 StartY=142 StartZ=0 EndX=132 EndY=142 EndZ=0
  constraints (43):
    c: Horizontal(g0)
    c: Vertical(g1)
    c: Coincident(g1,g0)
    c: DistanceY(g-1,g0) = 10
    c: DistanceX(g0,g0) = 114
    c: DistanceX(g-1,g0) = 18
    c: Radius(g2) = 37.5
    c: DistanceY(g-1,g2) = 37.5
    c: DistanceX(g2,g0) = 27
    c: Coincident(g3,g2)
    c: Radius(g3) = 23
    c: PointOnObject(g4,g3)
    c: Horizontal(g4)
    c: DistanceX(g4,g4) = 78
    c: Coincident(g5,g2)
    c: Coincident(g5,g4)
    c: Coincident(g6,g4)
    c: Coincident(g6,g2)
    c: Vertical(g6)
    c: Coincident(g7,g4)
    c: Vertical(g7)
    c: Coincident(g8,g7)
    c: Coincident(g8,g5)
    c: Tangent(g8,g3)
    c: DistanceY(g7,g7) = 33
    c: Vertical(g9)
    c: DistanceY(g4,g9) = 20
    c: Coincident(g10,g9)
    c: Horizontal(g10)
    c: Vertical(g11)
    c: Coincident(g10,g11)
    c: DistanceX(g10,g10) = 69
    c: Coincident(g12,g0)
    c: Vertical(g12)
    c: Coincident(g13,g12)
    c: Coincident(g13,g9)
    c: Horizontal(g13)
    c: Coincident(g14,g11)
    c: Horizontal(g14)
    c: Coincident(g14,g1)
    c: DistanceY(g1,g1) = 132
    c: Equal(g12,g1)
    c: DistanceX(g13,g13) = 10
FEATURE [PartDesign::Pad] Pad021  label="Corps droit interieur001"
  Length = 13
  Length2 = 100
  Placement = pos=(0,0,0) rot=(1,0,0;1.5708rad)
  Profile = -> Sketch053
  Type = 0
FEATURE [PartDesign::Pad] Pad020  label="Corps droite extérieur001"
  BaseFeature = -> Pad021
  Length = 5
  Length2 = 100
  Placement = pos=(0,0,0) rot=(1,0,0;1.5708rad)
  Profile = -> Sketch052
  Reversed = true
  Type = 0
FEATURE [PartDesign::Body] Body021  label="Corps droite001"
  Group = -> [Sketch053,Sketch052,Pad021,Pad020]
  Origin = -> Origin023
  Tip = -> Pad020
